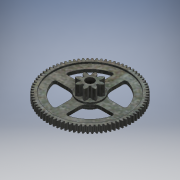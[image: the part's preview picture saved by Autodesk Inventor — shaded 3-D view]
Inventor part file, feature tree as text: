
AUTODESK INVENTOR PART (.ipt)
format: ipt  version: 2016 (Build 200138000, 138)  size: 2,431,488 bytes
history: native  units: mm
features: sketch x8, other x6, extrude x5, fillet x2, projected_geometry x2, hole x1
ambient origin geometry x8: Origin, YZ Plane, XZ Plane, XY Plane, X Axis, Y Axis, Z Axis, Center Point
bodies: Body1 (feature_tree)
feature tree (24):
  other  "ソリッド1"
  sketch  "スケッチ1"
  extrude  "押し出し1"  Depth=3.0mm TaperAngle=0.0deg
  extrude  "押し出し3"  Depth=12.0mm
  extrude  "押し出し4"  Depth=36.5mm
  sketch  "スケッチ8"
  extrude  "押し出し6"  Depth=0.75mm TaperAngle=0.0deg
  hole  "穴2"  [1 undecoded]
  extrude  "押し出し7"  Depth=36.5mm
  fillet  "フィレット1"  Radius=0.75mm
  fillet  "フィレット2"  Radius=5.0mm
  sketch  "スケッチ12"
  sketch  "スケッチ3"
  sketch  "スケッチ4"
  sketch  "スケッチ9"
  sketch  "スケッチ10"
  sketch  "スケッチ11"
  projected_geometry  "投影ループ1"
  projected_geometry  "投影ループ2"
  other  "断面エッジを投影2"
  other  "断面エッジを投影3"
  other  "断面エッジを投影5"
  other  "断面エッジを投影6"
  other  "断面エッジを投影7"
note: 1 required parameter value undecoded (feature->parameter linkage not recoverable at this tier; creation-order binding heuristic only, values carry confidence <= 0.55)
